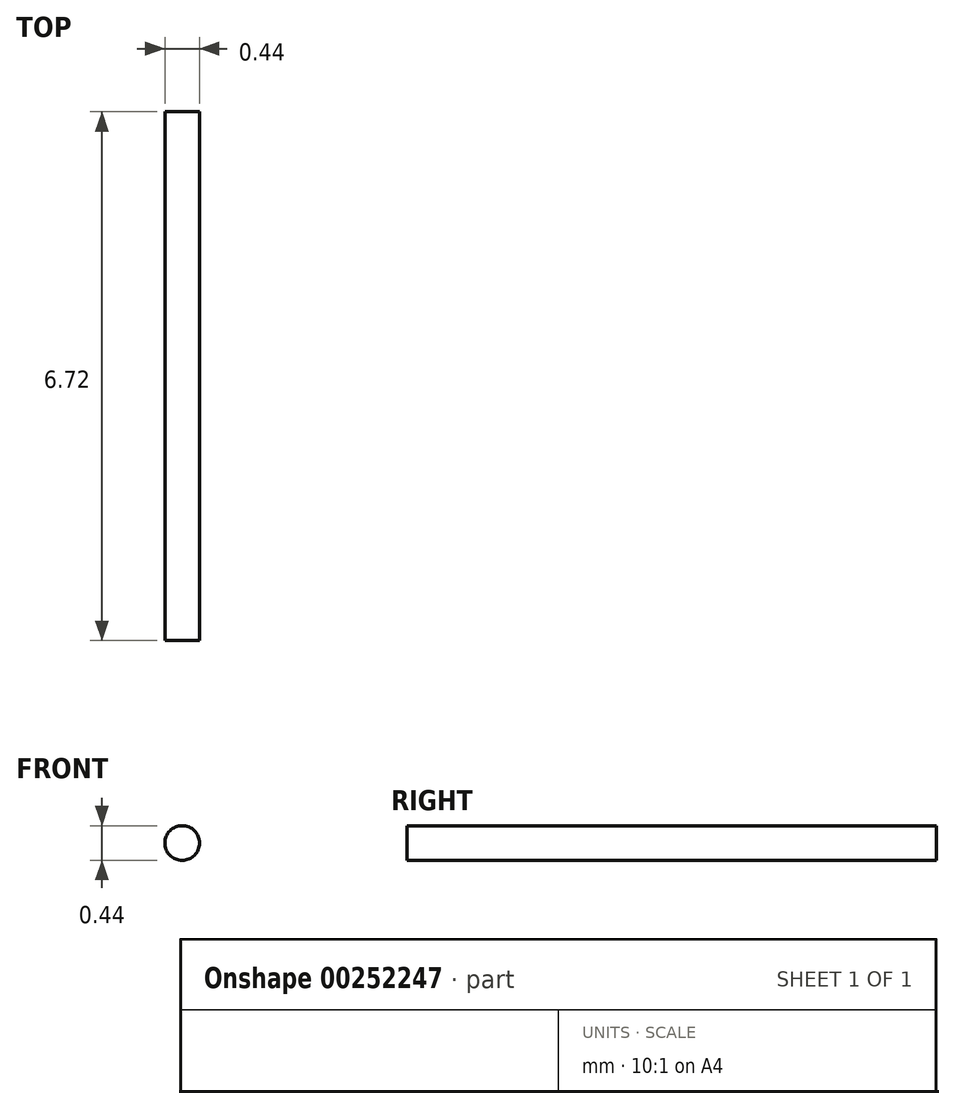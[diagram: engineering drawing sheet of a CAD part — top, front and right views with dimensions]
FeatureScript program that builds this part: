
annotation { "Feature Type Name" : "Feature", "Feature Type Description" : "" }
export const myFeature = defineFeature(function(context is Context, id is Id, definition is map)
    precondition{}
    {
        {
            var Q0;
            Q0=qCreatedBy(makeId("Front.planeOp"),FACE);
            var sketch = newSketch(context, id + "F0", { "sketchPlane" : qUnion([Q0])});
            skCircle(sketch, "E0", {"center": v(0, 0) * mm, "radius": 0.22 * mm});
            skSolve(sketch);
        }
        {
            var Q0;
            Q0 = qSketchRegion(id + "F0", true);
            extrude(context, id + "F1", {"entities" : qUnion([Q0]), "depth" : 6.72 * mm});
        }
    });
